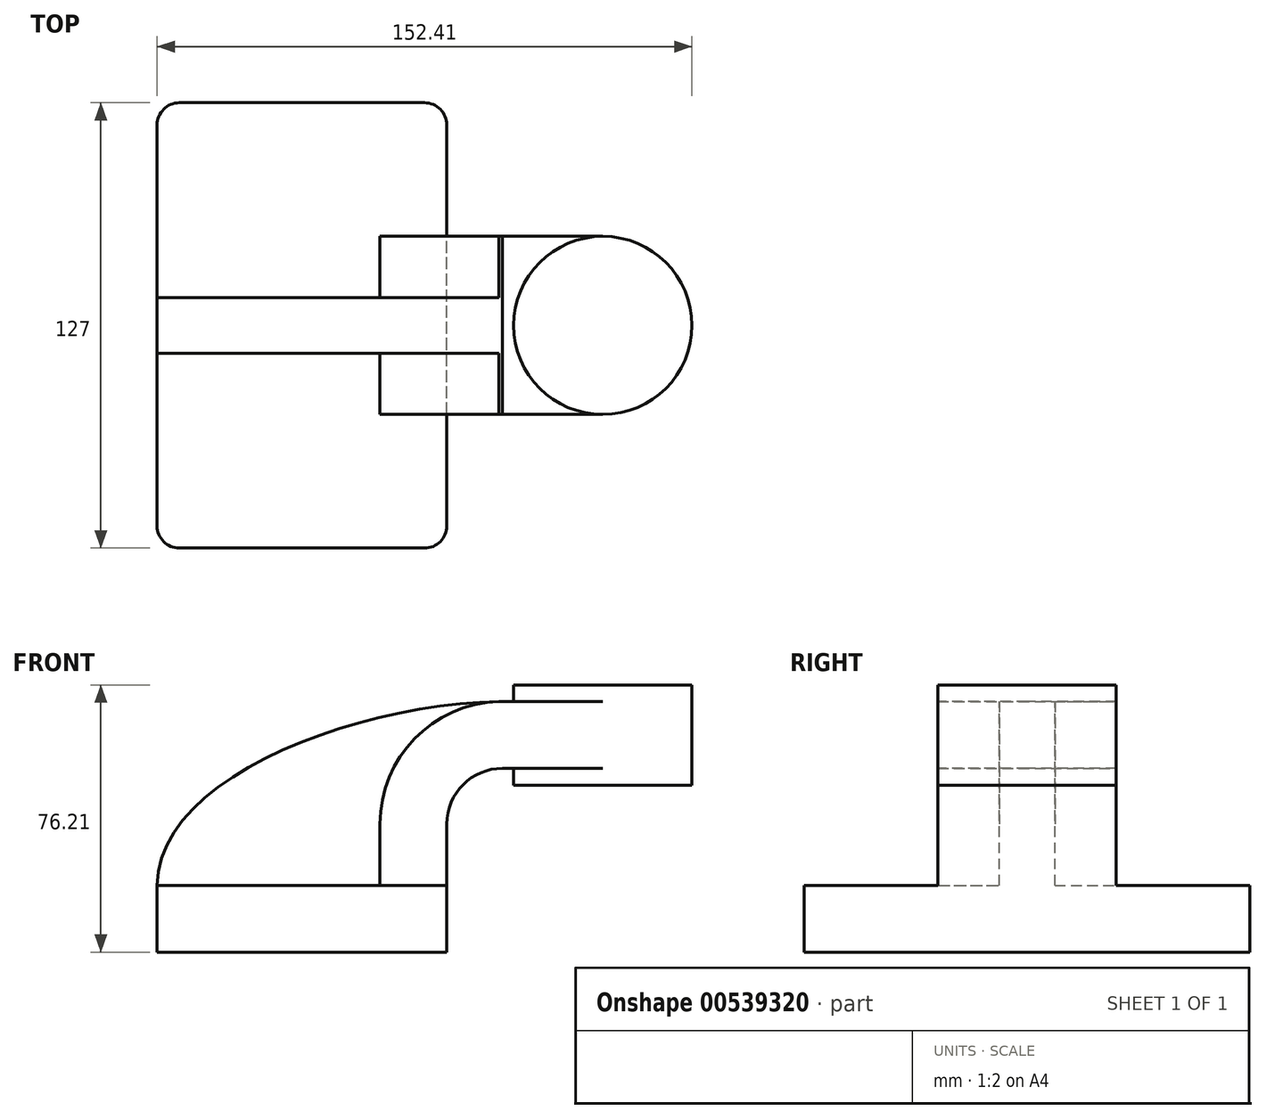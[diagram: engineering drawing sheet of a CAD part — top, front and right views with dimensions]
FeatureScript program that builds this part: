
annotation { "Feature Type Name" : "Feature", "Feature Type Description" : "" }
export const myFeature = defineFeature(function(context is Context, id is Id, definition is map)
    precondition{}
    {
        {
            var Q0;
            Q0=qCreatedBy(makeId("Front.planeOp"),FACE);
            var sketch = newSketch(context, id + "F0", { "sketchPlane" : qUnion([Q0])});
            skLineSegment(sketch, "E0.bottom", {"start": v(41.28, -9.52) * mm, "end": v(-41.27, -9.53) * mm});
            skLineSegment(sketch, "E0.top", {"start": v(41.27, 9.53) * mm, "end": v(-41.28, 9.53) * mm});
            skLineSegment(sketch, "E0.left", {"start": v(41.28, -9.52) * mm, "end": v(41.28, 9.53) * mm});
            skLineSegment(sketch, "E0.right", {"start": v(-41.27, -9.53) * mm, "end": v(-41.28, 9.53) * mm});
            skPoint(sketch, "E0.middle", {"position": v(0, 0) * mm});
            skLineSegment(sketch, "E1.bottom", {"start": v(60.32, 38.1) * mm, "end": v(111.12, 38.1) * mm});
            skLineSegment(sketch, "E1.top", {"start": v(60.32, 66.68) * mm, "end": v(111.12, 66.68) * mm});
            skLineSegment(sketch, "E1.left", {"start": v(60.32, 38.1) * mm, "end": v(60.32, 66.68) * mm});
            skLineSegment(sketch, "E1.right", {"start": v(111.12, 38.1) * mm, "end": v(111.12, 66.68) * mm});
            skPoint(sketch, "E1.middle", {"position": v(85.72, 52.39) * mm});
            skLineSegment(sketch, "E2", {"start": v(41.27, 9.53) * mm, "end": v(41.27, 27) * mm});
            skArc(sketch, "E3", {"start": v(41.27, 27) * mm, "mid": v(45.92, 38.23) * mm, "end": v(57.15, 42.88) * mm});
            skLineSegment(sketch, "E4", {"start": v(57.15, 42.88) * mm, "end": v(85.72, 42.88) * mm});
            skLineSegment(sketch, "E5.0", {"start": v(57.15, 61.93) * mm, "end": v(85.72, 61.93) * mm});
            skArc(sketch, "E5.1", {"start": v(22.23, 27) * mm, "mid": v(32.45, 51.7) * mm, "end": v(57.15, 61.93) * mm});
            skLineSegment(sketch, "E5.2", {"start": v(22.22, 9.53) * mm, "end": v(22.22, 27) * mm});
            skLineSegment(sketch, "E6", {"start": v(85.73, 38.1) * mm, "end": v(85.72, 66.68) * mm});
            skFitSpline(sketch, "E7", {"points": [v(-41.28, 9.53) * mm, v(57.15, 61.93) * mm], "startDerivative": vector(0.32, 92.33) * mm, "endDerivative": vector(125.01, 1.33) * mm});
            skSolve(sketch);
        }
        {
            var Q0;
            Q0=makeQuery(id+"F0.imprint","IMPRINT",FACE,{"disambiguationData":[TD([[makeQuery(id+"F0.imprint","IMPRINT",EDGE,{"derivedFrom":sQuery(id+"F0.wireOp",EDGE,"E0.bottom")}),-1.0]])]});
            extrude(context, id + "F1", {"entities" : qUnion([Q0]), "endBound" : BoundingType.SYMMETRIC, "depth" : 127 * mm, "offsetDistance" : 25.4 * mm});
        }
        {
            var Q0;
            {var subQ1=sQuery(id+"F0.wireOp",EDGE,"E2");Q0=makeQuery(id+"F0.imprint","IMPRINT",FACE,{"disambiguationData":[TD([[makeQuery(id+"F0.imprint","IMPRINT",EDGE,{"derivedFrom":subQ1}),1.0]])]});}
            var Q1;
            {var subQ0=sQuery(id+"F0.wireOp",EDGE,"E4");var subQ1=sQuery(id+"F0.wireOp",EDGE,"E1.left");var subQ2=makeQuery(id+"F0.imprint","INTERSECT",VERTEX,{"derivedFrom":[subQ1,subQ0]});Q1=makeQuery(id+"F0.imprint","IMPRINT",FACE,{"disambiguationData":[TD([[makeQuery(id+"F0.imprint","IMPRINT",EDGE,{"disambiguationData":[TD([[subQ2,-1.0]])],"derivedFrom":subQ1}),-1.0]])]});}
            extrude(context, id + "F2", {"entities" : qUnion([Q0, Q1]), "operationType" : NewBodyOperationType.ADD, "endBound" : BoundingType.SYMMETRIC, "depth" : 50.8 * mm, "offsetDistance" : 25.4 * mm});
        }
        {
            var Q0;
            {var subQ3=sQuery(id+"F0.wireOp",EDGE,"E5.2");Q0=makeQuery(id+"F0.imprint","IMPRINT",FACE,{"disambiguationData":[TD([[makeQuery(id+"F0.imprint","IMPRINT",EDGE,{"derivedFrom":subQ3}),1.0]])]});}
            extrude(context, id + "F3", {"entities" : qUnion([Q0]), "operationType" : NewBodyOperationType.ADD, "endBound" : BoundingType.SYMMETRIC, "depth" : 15.88 * mm, "offsetDistance" : 25.4 * mm});
        }
        {
            var Q0;
            {var subQ4=sQuery(id+"F0.wireOp",EDGE,"E1.right");Q0=makeQuery(id+"F0.imprint","IMPRINT",FACE,{"disambiguationData":[TD([[makeQuery(id+"F0.imprint","IMPRINT",EDGE,{"derivedFrom":subQ4}),1.0]])]});}
            var Q1;
            Q1=sQuery(id+"F0.wireOp",EDGE,"E6");
            revolve(context, id + "F4", {"operationType" : NewBodyOperationType.ADD, "entities" : qUnion([Q0]), "axis" : qUnion([Q1]), "revolveType" : RevolveType.FULL});
        }
        {
            var Q0;
            Q0=makeQuery(id+"F1.opExtrude","CAP_EDGE",EDGE,{"disambiguationData":[OSD([sQuery(id+"F0.wireOp",EDGE,"E0.left")])],"isStart":false});
            var Q1;
            Q1=makeQuery(id+"F1.opExtrude","CAP_EDGE",EDGE,{"disambiguationData":[OSD([sQuery(id+"F0.wireOp",EDGE,"E0.right")])],"isStart":false});
            var Q2;
            Q2=makeQuery(id+"F1.opExtrude","CAP_EDGE",EDGE,{"disambiguationData":[OSD([sQuery(id+"F0.wireOp",EDGE,"E0.left")])],"isStart":true});
            var Q3;
            Q3=makeQuery(id+"F1.opExtrude","CAP_EDGE",EDGE,{"disambiguationData":[OSD([sQuery(id+"F0.wireOp",EDGE,"E0.right")])],"isStart":true});
            fillet(context, id + "F5", {"entities" : qUnion([Q0, Q1, Q2, Q3]), "radius" : 6.35 * mm, "tangentPropagation" : true, "allowEdgeOverflow" : false});
        }
    });
